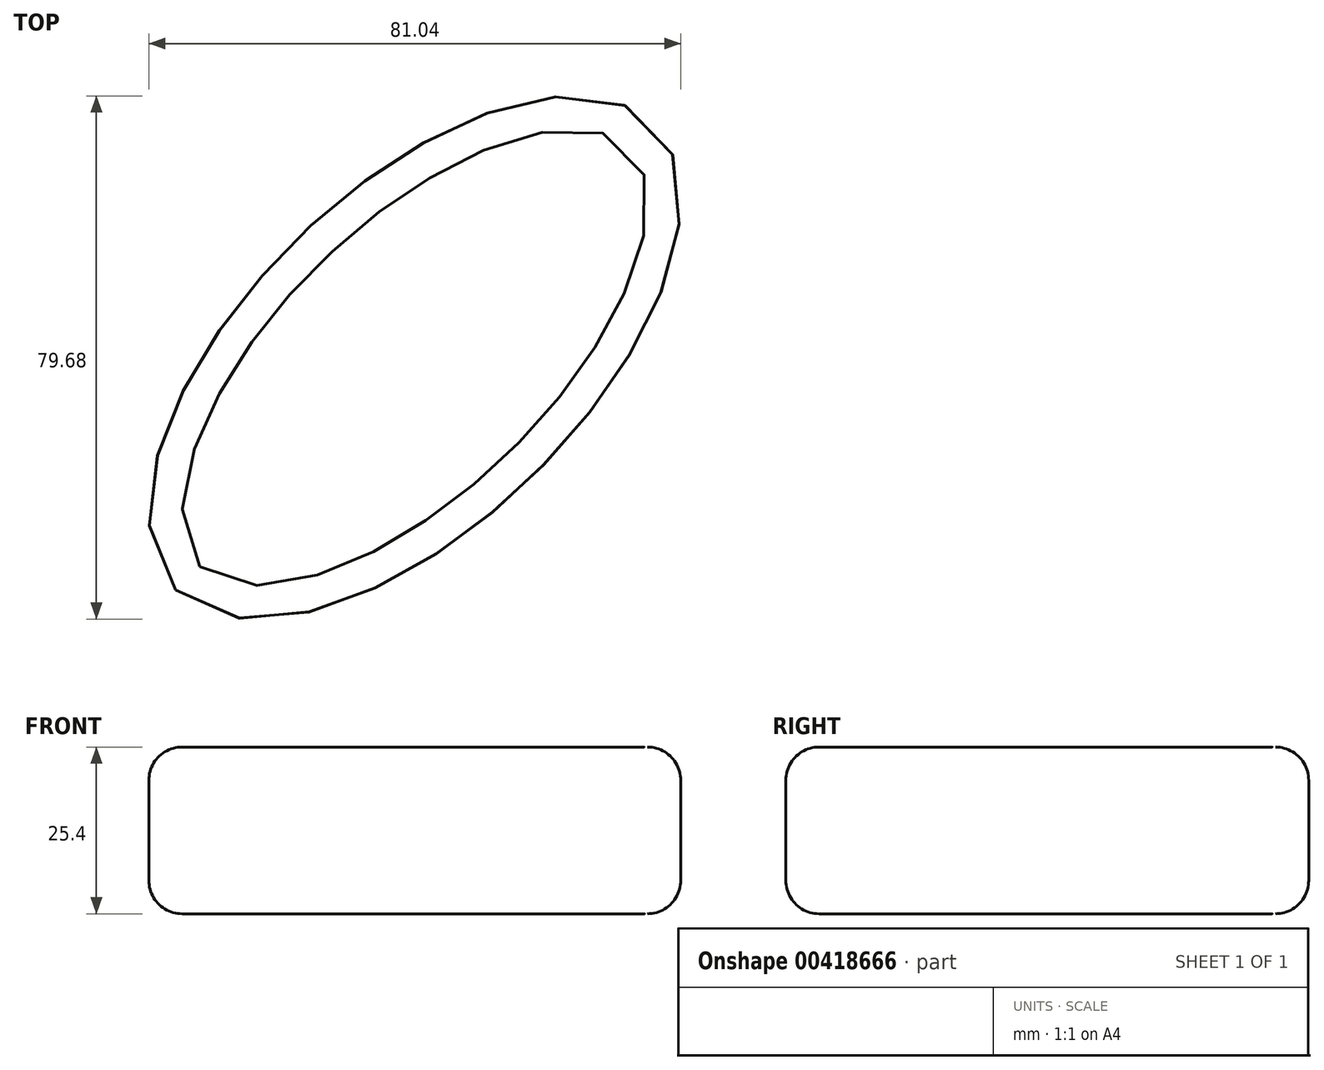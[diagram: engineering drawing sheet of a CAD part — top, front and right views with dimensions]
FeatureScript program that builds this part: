
annotation { "Feature Type Name" : "Feature", "Feature Type Description" : "" }
export const myFeature = defineFeature(function(context is Context, id is Id, definition is map)
    precondition{}
    {
        {
            var Q0;
            Q0=qCreatedBy(makeId("Top.planeOp"),FACE);
            var sketch = newSketch(context, id + "F0", { "sketchPlane" : qUnion([Q0])});
            skEllipse(sketch, "E0", {"center": v(0, 0) * mm, "majorRadius": 25.46 * mm, "minorRadius": 50.8 * mm, "majorAxis": v(-0.7, 0.72)});
            skSolve(sketch);
        }
        {
            var Q0;
            Q0 = qSketchRegion(id + "F0", true);
            extrude(context, id + "F1", {"entities" : qUnion([Q0]), "depth" : 25.4 * mm});
        }
        {
            var Q0;
            Q0=makeQuery(id+"F1.opExtrude","CAP_EDGE",EDGE,{"disambiguationData":[OSD([sQuery(id+"F0.wireOp",EDGE,"E0")])],"isStart":false});
            var Q1;
            Q1=makeQuery(id+"F1.opExtrude","CAP_EDGE",EDGE,{"disambiguationData":[OSD([sQuery(id+"F0.wireOp",EDGE,"E0")])],"isStart":true});
            fillet(context, id + "F2", {"entities" : qUnion([Q0, Q1]), "radius" : 5.08 * mm, "tangentPropagation" : true, "allowEdgeOverflow" : false});
        }
    });
